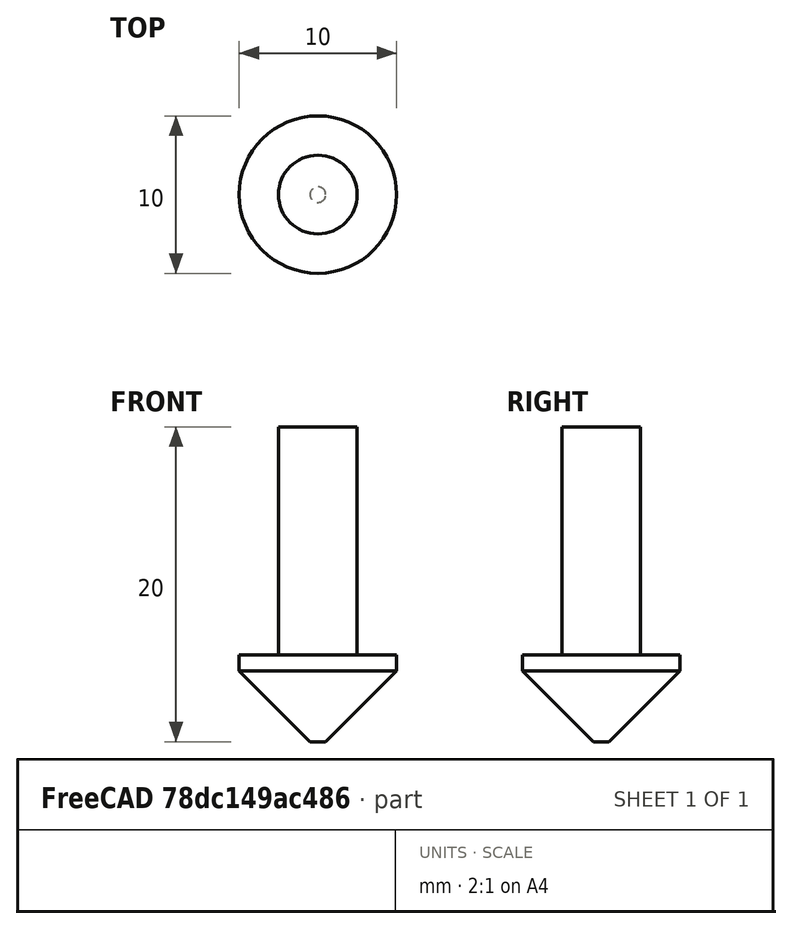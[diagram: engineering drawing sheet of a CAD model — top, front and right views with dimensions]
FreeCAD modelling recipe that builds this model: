
FCSTD DOCUMENT  (FreeCAD 0.21R32460 (Git))
Label: v-bit
License: Creative Commons Attribution 4.0
LicenseURL: https://creativecommons.org/licenses/by/4.0/
objects: Sketcher::SketchObject×1, PartDesign::Revolution×1, App::FeaturePython×1, PartDesign::Body×1
note: 4 computed .brp shape members not serialized (recipe doc carries the construction recipe); baked Part::Feature solids carry a one-line shape summary decoded from their .brp

FEATURE [Sketcher::SketchObject] Sketch
  FullyConstrained = true
  MapMode = 5
  Placement = pos=(0,0,0) rot=(1,0,0;1.5708rad)
  Support = -> [XZ_Plane]
  expr: Constraints[17] = <<Attributes>>.Diameter
  expr: Constraints[18] = <<Attributes>>.CuttingEdgeAngle
  expr: Constraints[19] = <<Attributes>>.Length
  expr: Constraints[22] = <<Attributes>>.ShankDiameter
  expr: Constraints[26] = <<Attributes>>.CuttingEdgeHeight
  expr: Constraints[28] = <<Attributes>>.TipDiameter
  sketch-geometry (12):
    g0: LineSegment StartX=0 StartY=20 StartZ=0 EndX=0 EndY=0 EndZ=0
    g1: LineSegment StartX=0 StartY=0 StartZ=0 EndX=0.5 EndY=0 EndZ=0
    g2: LineSegment StartX=0.5 StartY=0 StartZ=0 EndX=5 EndY=4.5 EndZ=0
    g3: LineSegment StartX=5 StartY=5.5 StartZ=0 EndX=2.5 EndY=5.49 EndZ=0
    g4: LineSegment StartX=2.5 StartY=5.49 StartZ=0 EndX=2.5 EndY=20 EndZ=0
    g5: LineSegment StartX=2.5 StartY=20 StartZ=0 EndX=0 EndY=20 EndZ=0
    g6: LineSegment StartX=-5 StartY=4.5 StartZ=0 EndX=5 EndY=4.5 EndZ=0
    g7: LineSegment StartX=5 StartY=4.5 StartZ=0 EndX=0.5 EndY=0 EndZ=0
    g8: LineSegment StartX=0.5 StartY=0 StartZ=0 EndX=-0.5 EndY=0 EndZ=0
    g9: LineSegment StartX=-0.5 StartY=0 StartZ=0 EndX=-5 EndY=4.5 EndZ=0
    g10: LineSegment StartX=2.5 StartY=20 StartZ=0 EndX=-2.5 EndY=20 EndZ=0
    g11: LineSegment StartX=5 StartY=4.5 StartZ=0 EndX=5 EndY=5.5 EndZ=0
  constraints (30):
    c: Vertical(g0)
    c: Coincident(g0,g1)
    c: Horizontal(g1)
    c: Coincident(g1,g2)
    c: Coincident(g3,g4)
    c: Vertical(g4)
    c: Coincident(g4,g5)
    c: Horizontal(g5)
    c: Coincident(g5,g0)
    c: Coincident(g6,g7)
    c: Coincident(g7,g8)
    c: Coincident(g8,g9)
    c: Coincident(g9,g6)
    c: Symmetric(g8,g7,g0)
    c: Coincident(g1,g7)
    c: Coincident(g2,g6)
    c: Symmetric(g2,g6,g0)
    c: DistanceX(g6,g6) = 10
    c: Angle(g2,g9) = 1.5708
    c: DistanceY(g0,g0) = 20
    c: Coincident(g10,g4)
    c: Symmetric(g10,g4,g-2)
    c: DistanceX(g10,g10) = 5
    c: Vertical(g11)
    c: Coincident(g3,g11)
    c: Coincident(g11,g2)
    c: DistanceY(g11,g11) = 1
    c: Coincident(g-1,g0)
    c: DistanceX(g8,g8) = 1
    c: DistanceY(g3,g3) = 0.01
FEATURE [PartDesign::Revolution] Revolution
  AllowMultiFace = false
  Angle = 360
  Axis = (0,-2e-16,1)
  Base = (0,0,0)
  Placement = pos=(0,0,0) rot=(1,0,0;1.5708rad)
  Profile = -> Sketch
  ReferenceAxis = -> Sketch [V_Axis]
  Reversed = true
FEATURE [App::FeaturePython] PropertyBag  label="Attributes"  # WARN: FeaturePython — macro-defined, semantics opaque (R4)
  Chipload = 0
  CustomPropertyGroups = Attributes | Shape
  CuttingEdgeAngle = 90
  CuttingEdgeHeight = 1
  Diameter = 10
  Flutes = 0
  Length = 20
  Material = 0
  ShankDiameter = 5
  TipDiameter = 1
FEATURE [PartDesign::Body] Body  label="V-Bit"
  Group = -> [Sketch,Revolution,PropertyBag]
  Origin = -> Origin
  Tip = -> Revolution
